# Revit family: IVLB_L4U_LF_Forsite 1150 PE
name_source: partatom
category: Lighting Fixtures
units: mm (PartAtom-declared; Revit-internal decimal feet)

## family parameters
Always vertical = Yes
Cut with Voids When Loaded = No
Light Source = Yes
OmniClass Number = 23.80.70.11.14.11
OmniClass Title = Downlights
Part Type = Normal
Room Calculation Point = Yes
Round Connector Dimension = Use Diameter
Shared = No
Work Plane-Based = No

## types (9) — shared parameters
Apparent Load = 68 VA
Assembly Code = 63.0
Calc_L1_Symbol = 12 mm  [stored 0.0393701 ft]
Calc_L2_Symbol = 1 mm  [stored 0.00328084 ft]
Color Filter = 16777215
Dimming Lamp Color Temperature Shift = <None>
ETIM Code = -
Emit Shape Visible in Rendering = No
Emit from Rectangle Length = 1136 mm  [stored 3.72703 ft]
Emit from Rectangle Width = 52 mm  [stored 0.170604 ft]
GTIN Code = -
H1 = 52 mm  [stored 0.170604 ft]
Housing_Material = Select RGB Value for different appearance
IK Value = -
IP Value = IP20
ISBN Code = -
IfcExportAs = IfcLightFixtureType
IfcExportType = USERDEFINED
L1 = 1150 mm  [stored 3.77297 ft]
L2 = 66 mm  [stored 0.216535 ft]
L3 = 7 mm  [stored 0.0229659 ft]
L4 = 1000 mm
LED Panel = Yes
Lamp = LED
Manufacturer = Light4U
Model = Forsite
Tilt Angle = 90.00°
Type Comments = 1150 PE
URL = www.light4u.com
Voltage = 230 V
Wattage Comments = 68

## per-type parameters (varying)
| type | Luminous Flux (lm) | Photometric Web File |
| Forsite 1150  8900lm_840 68W 30deg | 8900 lm | Forsite 1150  8900lm_840 68W 30deg.ies |
| Forsite 1150 8150lm_940 68W 90deg | 8150 lm | Forsite 1150 8150lm_940 68W 90deg.ies |
| Forsite 1150 8400lm_ 830 68W 60deg | 8400 lm | Forsite 1150 8400lm_ 830 68W 60deg.ies |
| Forsite 1150 8500lm_830 68W 30deg | 8500 lm | Forsite 1150 8500lm_830 68W 30deg.ies |
| Forsite 1150 8800lm_ 840 68W 60deg | 8800 lm | Forsite 1150 8800lm_ 840 68W 60deg.ies |
| Forsite 1150 9100lm_830 68W DA | 9100 lm | Forsite 1150 9100lm_830 68W DA.ies |
| Forsite 1150 9300lm_830 68W 90deg | 9300 lm | Forsite 1150 9300lm_830 68W 90deg.ies |
| Forsite 1150 9530lm_840 68W DA | 9533 lm | Forsite 1150 9530lm_840 68W DA.ies |
| Forsite 1150 9750lm_840 68W 90deg | 9750 lm | Forsite 1150 9750lm_840 68W 90deg.ies |

note: [stored X ft] marks values corroborated as IEEE doubles in the binary element streams (Revit-internal decimal feet)

## geometry (parser evidence)
native form markers: Sweep x5
no freeform markers — native parametric forms only
